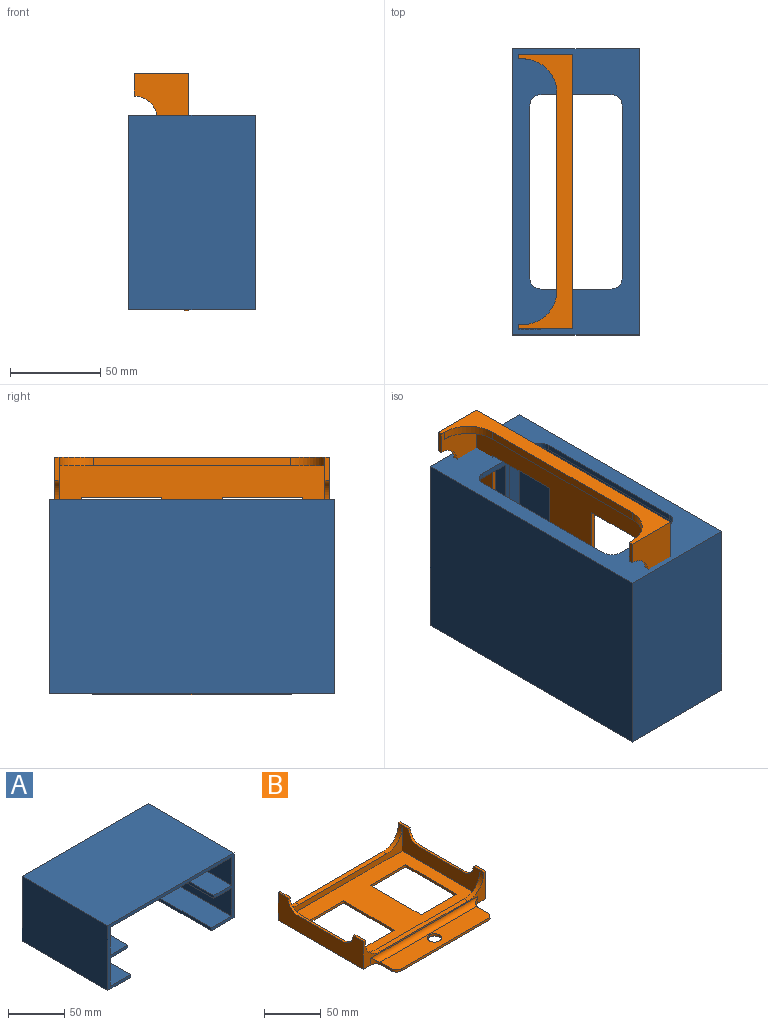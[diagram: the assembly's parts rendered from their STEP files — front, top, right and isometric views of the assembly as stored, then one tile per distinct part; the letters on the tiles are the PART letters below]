
ASSEMBLY  parts=2 mates=1
PART A: 31 faces, bbox 158.8x108x70.5 mm
  f0: plane 158.75x70.49mm, normal (0,-1,0), area 1233.9mm2, adj f1,f2,f3,f4,f5,f6,f7,f8
  f1: plane 158.75x107.95mm, normal (0,0,-1), area 9464.4mm2, adj f0,f7,f8,f20,f26,f27,f28,f29
  f2: plane 104.78x22.23mm, normal (0,0,1), area 2328.6mm2, adj f0,f10,f15,f17
  f3: plane 104.78x22.23mm, normal (0,0,-1), area 2328.6mm2, adj f0,f4,f15,f21
  f4: plane 104.78x30.48mm, normal (1,0,0), area 3193.5mm2, adj f0,f3,f11,f21
  f5: plane 104.78x30.48mm, normal (-1,0,0), area 3193.5mm2, adj f0,f11,f14,f21
  f6: plane 158.75x107.95mm, normal (0,0,1), area 17137.1mm2, adj f0,f7,f8,f20
  f7: plane 107.95x70.49mm, normal (-1,0,0), area 7608.9mm2, adj f0,f1,f6,f20
  f8: plane 107.95x70.49mm, normal (1,0,0), area 7608.9mm2, adj f0,f1,f6,f20
  f9: plane 152.4x104.78mm, normal (0,0,-1), area 15967.7mm2, adj f0,f10,f12,f17
  f10: plane 104.78x30.48mm, normal (1,0,0), area 3193.5mm2, adj f0,f2,f9,f17
  f11: plane 152.4x104.78mm, normal (0,0,1), area 8295mm2, adj f0,f4,f5,f21,f26,f27,f28,f29
  f12: plane 104.78x30.48mm, normal (-1,0,0), area 3193.5mm2, adj f0,f9,f13,f17
  f13: plane 104.78x22.23mm, normal (0,0,1), area 2328.6mm2, adj f0,f12,f16,f17
  f14: plane 104.78x22.23mm, normal (0,0,-1), area 2328.6mm2, adj f0,f5,f16,f21
  f15: plane 107.95x38.74mm, normal (1,0,0), area 455.6mm2, adj f0,f2,f3,f17,f20,f21,f22,f24
  f16: plane 107.95x38.74mm, normal (-1,0,0), area 455.6mm2, adj f0,f13,f14,f17,f20,f21,f23,f25
  f17: plane 152.4x30.48mm, normal (0,-1,0), area 2057.6mm2, adj f2,f9,f10,f12,f13,f15,f16,f19
  f18: plane 95.25x3.18mm, normal (0,0,1), area 302.4mm2, adj f20,f21,f24,f25
  f19: plane 95.25x3.18mm, normal (0,0,-1), area 302.4mm2, adj f17,f20,f22,f23
  f20: plane 158.75x70.49mm, normal (0,1,0), area 5671.7mm2, adj f1,f6,f7,f8,f15,f16,f18,f19
  f21: plane 152.4x30.48mm, normal (0,-1,0), area 2057.6mm2, adj f3,f4,f5,f11,f14,f15,f16,f18
  f22: cylinder r=6.35mm len=6.35mm, axis (0,-1,0), area 31.7mm2, adj f15,f17,f19,f20
  f23: cylinder r=6.35mm len=6.35mm, axis (0,1,0), area 31.7mm2, adj f16,f17,f19,f20
  f24: cylinder r=6.35mm len=6.35mm, axis (0,1,0), area 31.7mm2, adj f15,f18,f20,f21
  f25: cylinder r=6.35mm len=6.35mm, axis (0,-1,0), area 31.7mm2, adj f16,f18,f20,f21
  f26: plane 63.5x3.18mm, normal (1,0,0), area 201.6mm2, adj f0,f1,f11,f29
  f27: plane 76.2x3.18mm, normal (0,-1,0), area 241.9mm2, adj f1,f11,f29,f30
  f28: plane 63.5x3.18mm, normal (-1,0,0), area 201.6mm2, adj f0,f1,f11,f30
  f29: cylinder r=12.7mm len=12.7mm, axis (0,0,1), area 63.3mm2, adj f1,f11,f26,f27
  f30: cylinder r=12.7mm len=12.7mm, axis (0,0,-1), area 63.3mm2, adj f1,f11,f27,f28
PART B: 44 faces, bbox 152.4x131.8x30.2 mm
  f0: plane 12.7x2.38mm, normal (0,0,1), area 30.2mm2, adj f2,f4,f14,f36
  f1: plane 12.7x2.38mm, normal (0,0,1), area 30.2mm2, adj f3,f12,f14,f35
  f2: plane 106.38x27.79mm, normal (1,0,0), area 1754.8mm2, adj f0,f5,f6,f11,f13,f14,f16,f33
  f3: plane 106.38x27.79mm, normal (-1,0,0), area 1754.8mm2, adj f1,f5,f7,f11,f13,f14,f16,f32
  f4: plane 106.38x30.18mm, normal (-1,0,0), area 2250.7mm2, adj f0,f6,f8,f11,f14,f33,f36,f37
  f5: plane 147.64x96.83mm, normal (0,0,1), area 8649.8mm2, adj f2,f3,f13,f16,f24,f25,f26,f27
  f6: plane 12.7x2.38mm, normal (0,0,1), area 30.2mm2, adj f2,f4,f11,f37
  f7: plane 12.7x2.38mm, normal (0,0,1), area 30.2mm2, adj f3,f11,f12,f34
  f8: plane 152.4x131.78mm, normal (0,0,-1), area 13504.3mm2, adj f4,f9,f11,f12,f14,f18,f19,f20
  f9: plane 107.95x2.38mm, normal (0,-1,0), area 257.1mm2, adj f8,f10,f20,f22
  f10: plane 120.91x20.32mm, normal (0,0,1), area 2307.7mm2, adj f9,f18,f19,f20,f21,f22,f23,f38
  f11: plane 152.4x30.18mm, normal (0,1,0), area 1588.5mm2, adj f2,f3,f4,f6,f7,f8,f12,f17
  f12: plane 106.38x30.18mm, normal (1,0,0), area 2250.7mm2, adj f1,f7,f8,f11,f14,f32,f34,f35
  f13: plane 147.64x25.4mm, normal (0,1,0), area 1093.3mm2, adj f2,f3,f5,f15,f41,f42
  f14: plane 152.4x30.18mm, normal (0,-1,0), area 593.6mm2, adj f0,f1,f2,f3,f4,f8,f12,f15
  f15: plane 109.54x4.78mm, normal (0,0,1), area 523.1mm2, adj f13,f14,f41,f42
  f16: plane 147.64x25.4mm, normal (0,-1,0), area 1093.3mm2, adj f2,f3,f5,f17,f39,f40
  f17: plane 109.54x4.78mm, normal (0,0,1), area 523.1mm2, adj f11,f16,f39,f40
  f18: plane 12.7x2.38mm, normal (-1,0,0), area 30.2mm2, adj f8,f10,f19,f20
  f19: cylinder r=6.35mm len=7.46mm, axis (0,0,1), area 40.1mm2, adj f8,f10,f14,f18,f43
  f20: cylinder r=6.35mm len=6.35mm, axis (0,0,1), area 23.8mm2, adj f8,f9,f10,f18
  f21: plane 12.7x2.38mm, normal (1,0,0), area 30.2mm2, adj f8,f10,f22,f23
  f22: cylinder r=6.35mm len=6.35mm, axis (0,0,1), area 23.8mm2, adj f8,f9,f10,f21
  f23: cylinder r=6.35mm len=7.46mm, axis (0,0,1), area 40.1mm2, adj f8,f10,f14,f21,f43
  f24: plane 44.45x2.38mm, normal (0,1,0), area 105.8mm2, adj f5,f8,f25,f26
  f25: plane 63.5x2.38mm, normal (1,0,0), area 151.2mm2, adj f5,f8,f24,f27
  f26: plane 63.5x2.38mm, normal (-1,0,0), area 151.2mm2, adj f5,f8,f24,f27
  f27: plane 44.45x2.38mm, normal (0,-1,0), area 105.8mm2, adj f5,f8,f25,f26
  f28: plane 44.45x2.38mm, normal (0,-1,0), area 105.8mm2, adj f5,f8,f29,f30
  f29: plane 63.5x2.38mm, normal (-1,0,0), area 151.2mm2, adj f5,f8,f28,f31
  f30: plane 63.5x2.38mm, normal (1,0,0), area 151.2mm2, adj f5,f8,f28,f31
  f31: plane 44.45x2.38mm, normal (0,1,0), area 105.8mm2, adj f5,f8,f29,f30
  f32: plane 55.58x2.38mm, normal (0,0,1), area 132.3mm2, adj f3,f12,f34,f35
  f33: plane 55.58x2.38mm, normal (0,0,1), area 132.3mm2, adj f2,f4,f36,f37
  f34: cylinder r=12.7mm len=12.7mm, axis (1,0,0), area 47.5mm2, adj f3,f7,f12,f32
  f35: cylinder r=12.7mm len=12.7mm, axis (-1,0,0), area 47.5mm2, adj f1,f3,f12,f32
  f36: cylinder r=12.7mm len=12.7mm, axis (-1,0,0), area 47.5mm2, adj f0,f2,f4,f33
  f37: cylinder r=12.7mm len=12.7mm, axis (1,0,0), area 47.5mm2, adj f2,f4,f6,f33
  f38: cylinder r=6.35mm len=12.7mm, axis (0,0,1), area 95mm2, adj f8,f10
  f39: cylinder r=19.05mm len=19.05mm, axis (0,-1,0), area 142.9mm2, adj f3,f11,f16,f17
  f40: cylinder r=19.05mm len=19.05mm, axis (0,-1,0), area 142.9mm2, adj f2,f11,f16,f17
  f41: cylinder r=19.05mm len=19.05mm, axis (0,-1,0), area 142.9mm2, adj f2,f13,f14,f15
  f42: cylinder r=19.05mm len=19.05mm, axis (0,-1,0), area 142.9mm2, adj f3,f13,f14,f15
  f43: cylinder r=5.08mm len=133.35mm, axis (-1,0,0), area 1004.2mm2, adj f10,f14,f19,f23
PLACE A rot(axis=(0.58,-0.58,-0.58),120deg) t=(-23.63,73.85,-22.94)mm
PLACE B rot(axis=(0.58,-0.58,-0.58),120deg) t=(-25.52,73.85,-23.41)mm
MATE planar B.f4 <-> A.f4  axis (0,1,0) through (-40.61,150.05,1.99)mm
